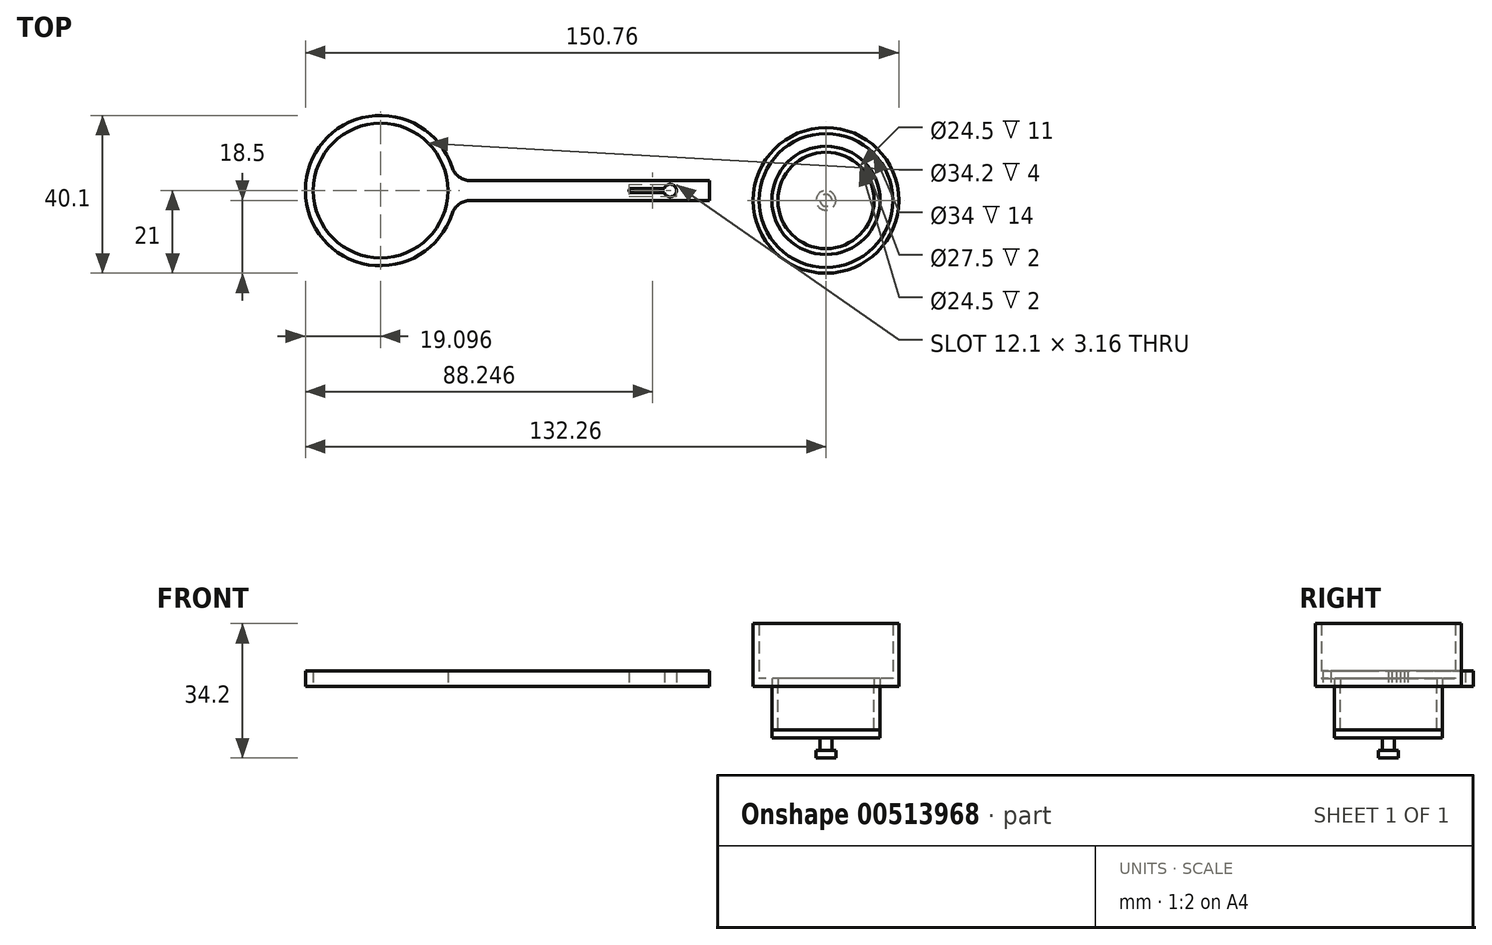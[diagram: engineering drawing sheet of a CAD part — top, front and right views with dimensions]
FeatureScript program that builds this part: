
annotation { "Feature Type Name" : "Feature", "Feature Type Description" : "" }
export const myFeature = defineFeature(function(context is Context, id is Id, definition is map)
    precondition{}
    {
        {
            var Q0;
            Q0=qCreatedBy(makeId("Top.planeOp"),FACE);
            var sketch = newSketch(context, id + "F0", { "sketchPlane" : qUnion([Q0])});
            skCircle(sketch, "E0", {"center": v(0, 0) * mm, "radius": 17 * mm});
            skCircle(sketch, "E1", {"center": v(0, 0) * mm, "radius": 12.25 * mm});
            skCircle(sketch, "E2", {"center": v(0, 0) * mm, "radius": 18.5 * mm});
            skCircle(sketch, "E3", {"center": v(0, 0) * mm, "radius": 13.75 * mm});
            skSolve(sketch);
        }
        {
            var Q0;
            Q0=makeQuery(id+"F0.imprint","IMPRINT",FACE,{"disambiguationData":[TD([[makeQuery(id+"F0.imprint","IMPRINT",EDGE,{"derivedFrom":sQuery(id+"F0.wireOp",EDGE,"E0")}),-1.0]])]});
            extrude(context, id + "F1", {"entities" : qUnion([Q0]), "depth" : 16 * mm});
        }
        {
            var Q0;
            Q0=makeQuery(id+"F0.imprint","IMPRINT",FACE,{"disambiguationData":[TD([[makeQuery(id+"F0.imprint","IMPRINT",EDGE,{"derivedFrom":sQuery(id+"F0.wireOp",EDGE,"E1")}),-1.0]])]});
            extrude(context, id + "F2", {"entities" : qUnion([Q0]), "oppositeDirection" : true, "depth" : 13 * mm});
        }
        {
            var Q0;
            Q0=makeQuery(id+"F0.imprint","IMPRINT",FACE,{"disambiguationData":[TD([[makeQuery(id+"F0.imprint","IMPRINT",EDGE,{"derivedFrom":sQuery(id+"F0.wireOp",EDGE,"E0")}),1.0]])]});
            extrude(context, id + "F3", {"entities" : qUnion([Q0]), "operationType" : NewBodyOperationType.ADD, "depth" : 2 * mm});
        }
        {
            var Q0;
            Q0=makeQuery(id+"F2.opExtrude","CAP_FACE",FACE,{"disambiguationData":[OSD([sQuery(id+"F0.wireOp",EDGE,"E1"),sQuery(id+"F0.wireOp",EDGE,"E3")])],"isStart":false});
            var sketch = newSketch(context, id + "F4", { "sketchPlane" : qUnion([Q0])});
            skCircle(sketch, "E4", {"center": v(0, 0) * mm, "radius": 13.76 * mm});
            skSolve(sketch);
        }
        {
            var Q0;
            Q0 = qSketchRegion(id + "F4", true);
            extrude(context, id + "F5", {"entities" : qUnion([Q0]), "operationType" : NewBodyOperationType.ADD, "oppositeDirection" : true, "depth" : 2 * mm});
        }
        {
            var Q0;
            Q0=makeQuery(id+"F0.imprint","IMPRINT",FACE,{"disambiguationData":[TD([[makeQuery(id+"F0.imprint","IMPRINT",EDGE,{"derivedFrom":sQuery(id+"F0.wireOp",EDGE,"E1")}),-1.0]])]});
            extrude(context, id + "F6", {"entities" : qUnion([Q0]), "depth" : 2 * mm});
        }
        {
            var Q0;
            Q0=makeQuery(id+"F5.boolean.opBoolean","MERGE",FACE,{"derivedFrom":[makeQuery(id+"F2.opExtrude","CAP_FACE",FACE,{"disambiguationData":[OSD([sQuery(id+"F0.wireOp",EDGE,"E1"),sQuery(id+"F0.wireOp",EDGE,"E3")])],"isStart":false}),makeQuery(id+"F5.opExtrude","CAP_FACE",FACE,{"disambiguationData":[OSD([sQuery(id+"F4.wireOp",EDGE,"E4")])],"isStart":true})]});
            var sketch = newSketch(context, id + "F7", { "sketchPlane" : qUnion([Q0])});
            skCircle(sketch, "E5", {"center": v(0, 0) * mm, "radius": 1.5 * mm});
            skSolve(sketch);
        }
        {
            var Q0;
            Q0=makeQuery(id+"F7.imprint","IMPRINT",FACE,{"disambiguationData":[TD([[makeQuery(id+"F7.imprint","IMPRINT",EDGE,{"derivedFrom":sQuery(id+"F7.wireOp",EDGE,"E5")}),1.0]])]});
            extrude(context, id + "F8", {"entities" : qUnion([Q0]), "operationType" : NewBodyOperationType.ADD, "depth" : 4.2 * mm, "offsetDistance" : 25 * mm});
        }
        {
            var Q0;
            Q0=makeQuery(id+"F8.opExtrude","CAP_FACE",FACE,{"disambiguationData":[OSD([sQuery(id+"F7.wireOp",EDGE,"E5")])],"isStart":false});
            var sketch = newSketch(context, id + "F9", { "sketchPlane" : qUnion([Q0])});
            skCircle(sketch, "E6", {"center": v(0, 0) * mm, "radius": 2.5 * mm});
            skSolve(sketch);
        }
        {
            var Q0;
            Q0=makeQuery(id+"F9.imprint","IMPRINT",FACE,{"disambiguationData":[TD([[makeQuery(id+"F9.imprint","IMPRINT",EDGE,{"derivedFrom":makeQuery(id+"F8.opExtrude","CAP_EDGE",EDGE,{"disambiguationData":[OSD([sQuery(id+"F7.wireOp",EDGE,"E5")])],"isStart":false})}),1.0]])]});
            var Q1;
            Q1=makeQuery(id+"F9.imprint","IMPRINT",FACE,{"disambiguationData":[TD([[makeQuery(id+"F9.imprint","IMPRINT",EDGE,{"derivedFrom":sQuery(id+"F9.wireOp",EDGE,"E6")}),1.0]])]});
            extrude(context, id + "F10", {"entities" : qUnion([Q0, Q1]), "operationType" : NewBodyOperationType.ADD, "endBound" : BoundingType.SYMMETRIC, "depth" : 2 * mm});
        }
        {
            var Q0;
            Q0=qCreatedBy(makeId("Top.planeOp"),FACE);
            var sketch = newSketch(context, id + "F11", { "sketchPlane" : qUnion([Q0])});
            skLineSegment(sketch, "E7.bottom", {"start": v(-29.56, 0) * mm, "end": v(-94.56, 0) * mm});
            skLineSegment(sketch, "E7.top", {"start": v(-29.56, 5) * mm, "end": v(-94.56, 5) * mm});
            skLineSegment(sketch, "E7.left", {"start": v(-29.56, 0) * mm, "end": v(-29.56, 5) * mm});
            skLineSegment(sketch, "E7.right", {"start": v(-94.56, 0) * mm, "end": v(-94.56, 5) * mm});
            skCircle(sketch, "E8", {"center": v(-39.56, 2.5) * mm, "radius": 1.6 * mm});
            skLineSegment(sketch, "E9", {"start": v(-39.56, 2.5) * mm, "end": v(-49.56, 2.5) * mm});
            skArc(sketch, "E10.0.startCap", {"start": v(-39.56, 3) * mm, "mid": v(-39.06, 2.5) * mm, "end": v(-39.56, 2) * mm});
            skArc(sketch, "E10.0.endCap", {"start": v(-49.56, 2) * mm, "mid": v(-50.06, 2.5) * mm, "end": v(-49.56, 3) * mm});
            skLineSegment(sketch, "E10.0.left", {"start": v(-39.56, 2) * mm, "end": v(-49.56, 2) * mm});
            skLineSegment(sketch, "E10.0.right", {"start": v(-39.56, 3) * mm, "end": v(-49.56, 3) * mm});
            skCircle(sketch, "E11", {"center": v(-113.16, 2.5) * mm, "radius": 17.1 * mm});
            skCircle(sketch, "E12", {"center": v(-113.16, 2.5) * mm, "radius": 19.1 * mm});
            skSolve(sketch);
        }
        {
            var Q0;
            {var subQ0=sQuery(id+"F11.wireOp",EDGE,"E7.right");Q0=makeQuery(id+"F11.imprint","IMPRINT",FACE,{"disambiguationData":[TD([[makeQuery(id+"F11.imprint","IMPRINT",EDGE,{"derivedFrom":subQ0}),1.0]])]});}
            var Q1;
            {var subQ5=sQuery(id+"F11.wireOp",EDGE,"E7.left");Q1=makeQuery(id+"F11.imprint","IMPRINT",FACE,{"disambiguationData":[TD([[makeQuery(id+"F11.imprint","IMPRINT",EDGE,{"derivedFrom":subQ5}),1.0]])]});}
            var Q2;
            {var subQ0=sQuery(id+"F11.wireOp",EDGE,"E7.right");Q2=makeQuery(id+"F11.imprint","IMPRINT",FACE,{"disambiguationData":[TD([[makeQuery(id+"F11.imprint","IMPRINT",EDGE,{"derivedFrom":subQ0}),-1.0]])]});}
            extrude(context, id + "F12", {"entities" : qUnion([Q0, Q1, Q2]), "depth" : 4 * mm, "offsetDistance" : 25 * mm});
        }
        {
            var Q0;
            Q0=makeQuery(id+"F12.opExtrude","SWEPT_EDGE",EDGE,{"disambiguationData":[OSD([sQuery(id+"F11.wireOp",EDGE,"E7.top"),sQuery(id+"F11.wireOp",EDGE,"E12")])]});
            var Q1;
            Q1=makeQuery(id+"F12.opExtrude","SWEPT_EDGE",EDGE,{"disambiguationData":[OSD([sQuery(id+"F11.wireOp",EDGE,"E7.bottom"),sQuery(id+"F11.wireOp",EDGE,"E12")])]});
            fillet(context, id + "F13", {"entities" : qUnion([Q0, Q1]), "radius" : 5 * mm, "tangentPropagation" : true, "allowEdgeOverflow" : false});
        }
    });
